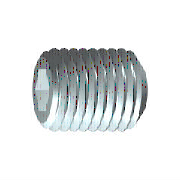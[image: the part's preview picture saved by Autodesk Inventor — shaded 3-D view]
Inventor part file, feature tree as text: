
AUTODESK INVENTOR PART (.ipt)
format: ipt  version: 2015 (Build 190159000, 159)  size: 177,664 bytes
history: native  units: mm (DEFAULTED — no unit token found)
features: sketch x2, extrude x1, other x1, plane x1
ambient origin geometry x8: Origin, YZ Plane, XZ Plane, XY Plane, X Axis, Y Axis, Z Axis, Center Point
bodies: Solid1 (feature_tree), Body (feature_tree)
feature tree (5):
  extrude  "Slot"  TaperAngle=60.0deg  [1 undecoded]
  other  "Work Axis1"
  plane  "Work Plane1"
  sketch  "Sketch1"  dims[d0=2.5mm d1=60.0deg]
  sketch  "Sketch2"  dims[d2=4.0mm d3=2.309401mm d6=90.0deg d4=0.0mm d5=6.0mm d21=10.0mm d7=0.0mm d8=6.0mm d9=0.0mm d10=0.429415mm d11=45.0deg d12=0.429415mm d13=45.0deg d34=0.429415mm d35=0.429415mm d36=0.0mm d37=0.0mm]
note: 1 required parameter value undecoded (feature->parameter linkage not recoverable at this tier; creation-order binding heuristic only, values carry confidence <= 0.55)
